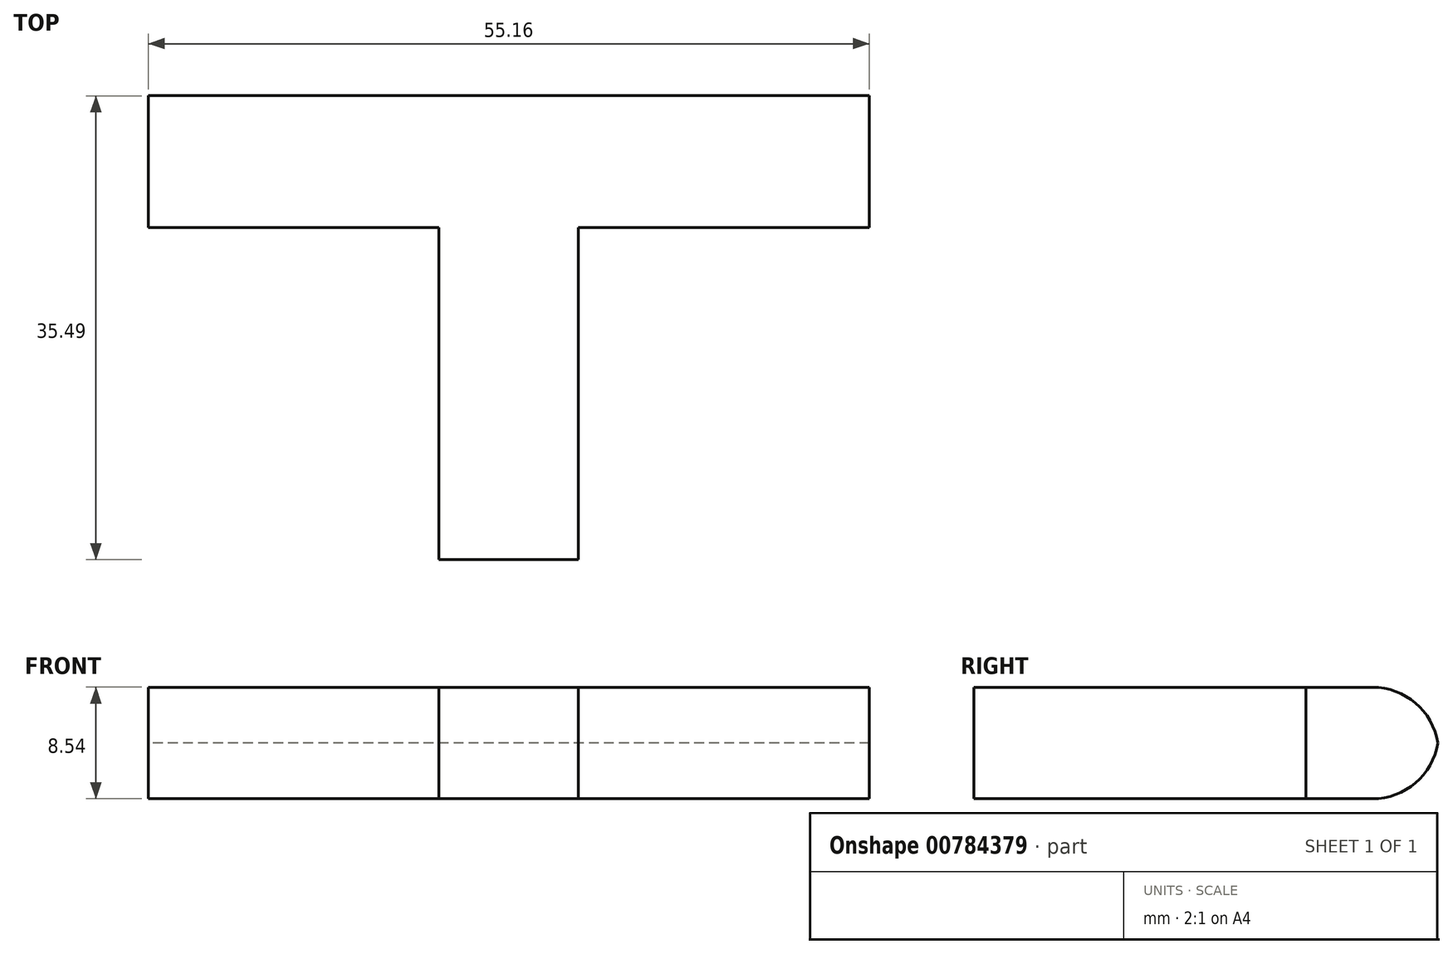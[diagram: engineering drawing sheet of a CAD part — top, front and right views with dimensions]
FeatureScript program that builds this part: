
annotation { "Feature Type Name" : "Feature", "Feature Type Description" : "" }
export const myFeature = defineFeature(function(context is Context, id is Id, definition is map)
    precondition{}
    {
        {
            var Q0;
            Q0=qCreatedBy(makeId("Front.planeOp"),FACE);
            var sketch = newSketch(context, id + "F0", { "sketchPlane" : qUnion([Q0])});
            skLineSegment(sketch, "E0.bottom", {"start": v(5.33, -4.27) * mm, "end": v(-5.33, -4.27) * mm});
            skLineSegment(sketch, "E0.top", {"start": v(5.33, 4.27) * mm, "end": v(-5.33, 4.27) * mm});
            skLineSegment(sketch, "E0.left", {"start": v(5.33, -4.27) * mm, "end": v(5.33, 4.27) * mm});
            skLineSegment(sketch, "E0.right", {"start": v(-5.33, -4.27) * mm, "end": v(-5.33, 4.27) * mm});
            skPoint(sketch, "E0.middle", {"position": v(0, 0) * mm});
            skSolve(sketch);
        }
        {
            var Q0;
            Q0=makeQuery(id+"F0.imprint","IMPRINT",FACE,{"disambiguationData":[TD([[makeQuery(id+"F0.imprint","IMPRINT",EDGE,{"derivedFrom":sQuery(id+"F0.wireOp",EDGE,"E0.bottom")}),-1.0]])]});
            extrude(context, id + "F1", {"entities" : qUnion([Q0]), "depth" : 25.4 * mm, "offsetDistance" : 25.4 * mm});
        }
        {
            var Q0;
            Q0=makeQuery(id+"F1.opExtrude","CAP_FACE",FACE,{"disambiguationData":[OSD([sQuery(id+"F0.wireOp",EDGE,"E0.bottom"),sQuery(id+"F0.wireOp",EDGE,"E0.top"),sQuery(id+"F0.wireOp",EDGE,"E0.left"),sQuery(id+"F0.wireOp",EDGE,"E0.right")])],"isStart":true});
            var sketch = newSketch(context, id + "F2", { "sketchPlane" : qUnion([Q0])});
            skLineSegment(sketch, "E1.bottom", {"start": v(27.58, -4.27) * mm, "end": v(-27.58, -4.27) * mm});
            skLineSegment(sketch, "E1.top", {"start": v(27.58, 4.27) * mm, "end": v(-27.58, 4.27) * mm});
            skLineSegment(sketch, "E1.left", {"start": v(27.58, -4.27) * mm, "end": v(27.58, 4.27) * mm});
            skLineSegment(sketch, "E1.right", {"start": v(-27.58, -4.27) * mm, "end": v(-27.58, 4.27) * mm});
            skPoint(sketch, "E1.middle", {"position": v(0, 0) * mm});
            skSolve(sketch);
        }
        {
            var Q0;
            {var subQ2=sQuery(id+"F2.wireOp",EDGE,"E1.right");Q0=makeQuery(id+"F2.imprint","IMPRINT",FACE,{"disambiguationData":[TD([[makeQuery(id+"F2.imprint","IMPRINT",EDGE,{"derivedFrom":subQ2}),-1.0]])]});}
            var Q1;
            {var subQ1=makeQuery(id+"F1.opExtrude","CAP_EDGE",EDGE,{"disambiguationData":[OSD([sQuery(id+"F0.wireOp",EDGE,"E0.left")])],"isStart":true});Q1=makeQuery(id+"F2.imprint","IMPRINT",FACE,{"disambiguationData":[TD([[makeQuery(id+"F2.imprint","IMPRINT",EDGE,{"derivedFrom":subQ1}),-1.0]])]});}
            var Q2;
            {var subQ2=sQuery(id+"F2.wireOp",EDGE,"E1.left");Q2=makeQuery(id+"F2.imprint","IMPRINT",FACE,{"disambiguationData":[TD([[makeQuery(id+"F2.imprint","IMPRINT",EDGE,{"derivedFrom":subQ2}),1.0]])]});}
            extrude(context, id + "F3", {"entities" : qUnion([Q0, Q1, Q2]), "operationType" : NewBodyOperationType.ADD, "depth" : 10.16 * mm, "offsetDistance" : 25.4 * mm});
        }
        {
            var Q0;
            Q0=makeQuery(id+"F3.opExtrude","CAP_EDGE",EDGE,{"disambiguationData":[OSD([sQuery(id+"F2.wireOp",EDGE,"E1.top")])],"isStart":false});
            var Q1;
            Q1=makeQuery(id+"F3.opExtrude","CAP_EDGE",EDGE,{"disambiguationData":[OSD([sQuery(id+"F2.wireOp",EDGE,"E1.bottom")])],"isStart":false});
            var Q2;
            {var subQ0=sQuery(id+"F2.wireOp",EDGE,"E1.top");Q2=makeQuery(id+"F3.boolean.opBoolean","SPLIT",EDGE,{"disambiguationData":[TD([makeQuery(id+"F1.opExtrude","SWEPT_FACE",FACE,{"disambiguationData":[OSD([sQuery(id+"F0.wireOp",EDGE,"E0.left")])]})])],"derivedFrom":makeQuery(id+"F3.opExtrude","CAP_EDGE",EDGE,{"disambiguationData":[OSD([subQ0])],"isStart":true})});}
            var Q3;
            {var subQ0=sQuery(id+"F2.wireOp",EDGE,"E1.bottom");Q3=makeQuery(id+"F3.boolean.opBoolean","SPLIT",EDGE,{"disambiguationData":[TD([makeQuery(id+"F1.opExtrude","SWEPT_FACE",FACE,{"disambiguationData":[OSD([sQuery(id+"F0.wireOp",EDGE,"E0.left")])]})])],"derivedFrom":makeQuery(id+"F3.opExtrude","CAP_EDGE",EDGE,{"disambiguationData":[OSD([subQ0])],"isStart":true})});}
            var Q4;
            {var subQ1=sQuery(id+"F2.wireOp",EDGE,"E1.bottom");Q4=makeQuery(id+"F3.boolean.opBoolean","SPLIT",EDGE,{"disambiguationData":[TD([makeQuery(id+"F1.opExtrude","SWEPT_FACE",FACE,{"disambiguationData":[OSD([sQuery(id+"F0.wireOp",EDGE,"E0.right")])]})])],"derivedFrom":makeQuery(id+"F3.opExtrude","CAP_EDGE",EDGE,{"disambiguationData":[OSD([subQ1])],"isStart":true})});}
            var Q5;
            {var subQ0=sQuery(id+"F2.wireOp",EDGE,"E1.top");Q5=makeQuery(id+"F3.boolean.opBoolean","SPLIT",EDGE,{"disambiguationData":[TD([makeQuery(id+"F1.opExtrude","SWEPT_FACE",FACE,{"disambiguationData":[OSD([sQuery(id+"F0.wireOp",EDGE,"E0.right")])]})])],"derivedFrom":makeQuery(id+"F3.opExtrude","CAP_EDGE",EDGE,{"disambiguationData":[OSD([subQ0])],"isStart":true})});}
            fillet(context, id + "F4", {"entities" : qUnion([Q0, Q1, Q2, Q3, Q4, Q5]), "radius" : 5.08 * mm, "tangentPropagation" : true, "allowEdgeOverflow" : false});
        }
    });
